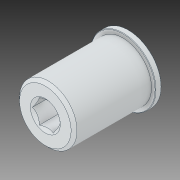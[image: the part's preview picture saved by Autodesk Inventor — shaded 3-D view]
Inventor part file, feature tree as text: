
AUTODESK INVENTOR PART (.ipt)
format: ipt  version: 2019 (Build 230136000, 136)  size: 139,776 bytes
history: native  units: in
note: dims shown in document units (in); Inventor stores cm internally (conversion verified against a paired STEP export)
features: chamfer x1
ambient origin geometry x8: Origin, YZ Plane, XZ Plane, XY Plane, X Axis, Y Axis, Z Axis, Center Point
bodies: Solid1 (feature_tree)
feature tree (1):
  chamfer  "Chamfer5"  [1 undecoded]
note: 1 required parameter value undecoded (feature->parameter linkage not recoverable at this tier; creation-order binding heuristic only, values carry confidence <= 0.55)
